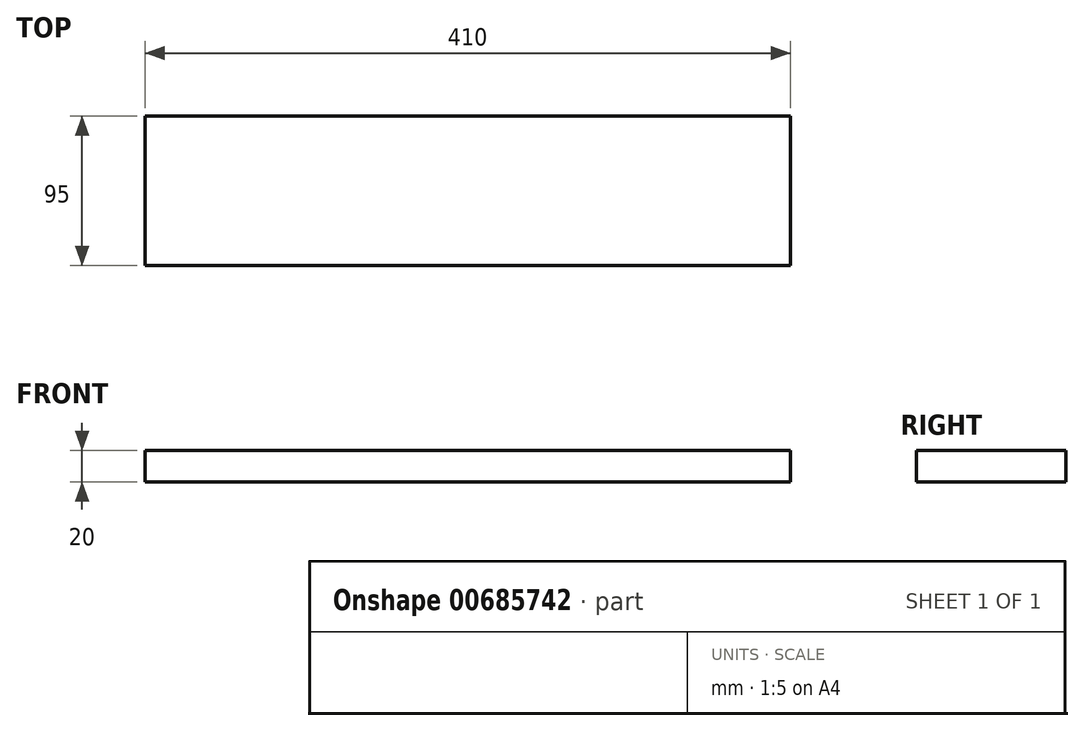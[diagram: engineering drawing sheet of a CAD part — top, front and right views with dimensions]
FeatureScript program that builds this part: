
annotation { "Feature Type Name" : "Feature", "Feature Type Description" : "" }
export const myFeature = defineFeature(function(context is Context, id is Id, definition is map)
    precondition{}
    {
        {
            var Q0;
            Q0=qCreatedBy(makeId("Right.planeOp"),FACE);
            var sketch = newSketch(context, id + "F0", { "sketchPlane" : qUnion([Q0])});
            skLineSegment(sketch, "E0.bottom", {"start": v(47.5, 10) * mm, "end": v(-47.5, 10) * mm});
            skLineSegment(sketch, "E0.top", {"start": v(47.5, -10) * mm, "end": v(-47.5, -10) * mm});
            skLineSegment(sketch, "E0.left", {"start": v(47.5, 10) * mm, "end": v(47.5, -10) * mm});
            skLineSegment(sketch, "E0.right", {"start": v(-47.5, 10) * mm, "end": v(-47.5, -10) * mm});
            skPoint(sketch, "E0.middle", {"position": v(0, 0) * mm});
            skSolve(sketch);
        }
        {
            var Q0;
            Q0=qSketchRegion(id+"F0",true);
            extrude(context, id + "F1", {"entities" : qUnion([Q0]), "endBound" : BoundingType.SYMMETRIC, "depth" : 410 * mm, "offsetDistance" : 25 * mm});
        }
    });
